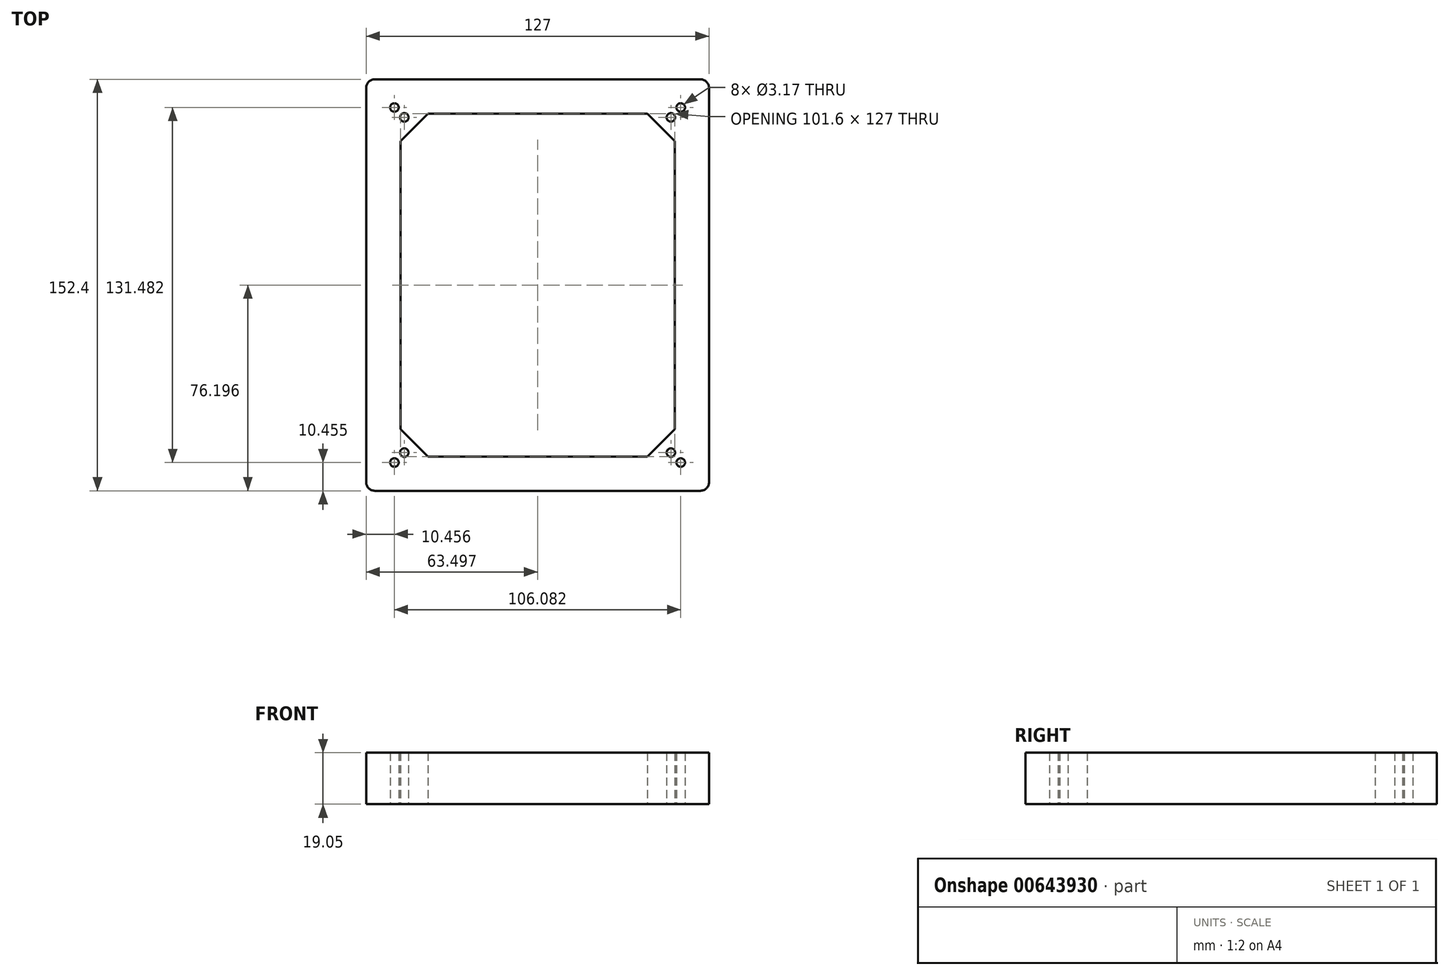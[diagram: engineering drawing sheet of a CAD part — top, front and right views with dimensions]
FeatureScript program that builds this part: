
annotation { "Feature Type Name" : "Feature", "Feature Type Description" : "" }
export const myFeature = defineFeature(function(context is Context, id is Id, definition is map)
    precondition{}
    {
        {
            var Q0;
            Q0=qCreatedBy(makeId("Top.planeOp"),FACE);
            var sketch = newSketch(context, id + "F0", { "sketchPlane" : qUnion([Q0])});
            skLineSegment(sketch, "E0.bottom", {"start": v(-60.12, 76.46) * mm, "end": v(60.53, 76.46) * mm});
            skLineSegment(sketch, "E0.top", {"start": v(-60.12, -75.94) * mm, "end": v(60.53, -75.94) * mm});
            skLineSegment(sketch, "E0.left", {"start": v(-63.3, 73.28) * mm, "end": v(-63.3, -72.77) * mm});
            skLineSegment(sketch, "E0.right", {"start": v(63.7, 73.28) * mm, "end": v(63.7, -72.77) * mm});
            skPoint(sketch, "E0.middle", {"position": v(0.2, 0.26) * mm});
            skLineSegment(sketch, "E1.bottom", {"start": v(-53.77, 70.1) * mm, "end": v(54.18, 70.1) * mm});
            skLineSegment(sketch, "E1.top", {"start": v(-53.77, -69.6) * mm, "end": v(54.18, -69.6) * mm});
            skLineSegment(sketch, "E1.left", {"start": v(-56.94, 66.93) * mm, "end": v(-56.94, -66.42) * mm});
            skLineSegment(sketch, "E1.right", {"start": v(57.36, 66.93) * mm, "end": v(57.36, -66.42) * mm});
            skLineSegment(sketch, "E2.bottom", {"start": v(-47.42, 63.76) * mm, "end": v(47.83, 63.76) * mm});
            skLineSegment(sketch, "E2.top", {"start": v(-47.42, -63.24) * mm, "end": v(48.46, -63.24) * mm});
            skLineSegment(sketch, "E2.left", {"start": v(-50.6, 60.58) * mm, "end": v(-50.6, -60.07) * mm});
            skLineSegment(sketch, "E2.right", {"start": v(51, 60.58) * mm, "end": v(51, -60.7) * mm});
            skPoint(sketch, "E3.visualSharp", {"position": v(-56.94, 70.1) * mm});
            skArc(sketch, "E3.filletArc", {"start": v(-53.77, 70.1) * mm, "mid": v(-56.01, 69.18) * mm, "end": v(-56.94, 66.93) * mm});
            skPoint(sketch, "E4.visualSharp", {"position": v(57.36, 70.1) * mm});
            skArc(sketch, "E4.filletArc", {"start": v(57.36, 66.93) * mm, "mid": v(56.43, 69.18) * mm, "end": v(54.18, 70.1) * mm});
            skPoint(sketch, "E5.visualSharp", {"position": v(57.36, -69.6) * mm});
            skArc(sketch, "E5.filletArc", {"start": v(54.18, -69.6) * mm, "mid": v(56.43, -68.66) * mm, "end": v(57.36, -66.42) * mm});
            skPoint(sketch, "E6.visualSharp", {"position": v(-56.94, -69.6) * mm});
            skArc(sketch, "E6.filletArc", {"start": v(-56.94, -66.42) * mm, "mid": v(-56.01, -68.66) * mm, "end": v(-53.77, -69.6) * mm});
            skPoint(sketch, "E7.visualSharp", {"position": v(51, 63.76) * mm});
            skArc(sketch, "E7.filletArc", {"start": v(51, 60.58) * mm, "mid": v(50.08, 62.83) * mm, "end": v(47.83, 63.76) * mm});
            skPoint(sketch, "E8.visualSharp", {"position": v(51, -63.24) * mm});
            skArc(sketch, "E8.filletArc", {"start": v(48.46, -63.24) * mm, "mid": v(50.26, -62.5) * mm, "end": v(51, -60.7) * mm});
            skPoint(sketch, "E9.visualSharp", {"position": v(-50.6, -63.24) * mm});
            skArc(sketch, "E9.filletArc", {"start": v(-50.6, -60.07) * mm, "mid": v(-49.66, -62.31) * mm, "end": v(-47.42, -63.24) * mm});
            skArc(sketch, "E10.filletArc", {"start": v(-47.42, 63.76) * mm, "mid": v(-49.66, 62.83) * mm, "end": v(-50.6, 60.58) * mm});
            skPoint(sketch, "E11.visualSharp", {"position": v(-63.3, 76.46) * mm});
            skArc(sketch, "E11.filletArc", {"start": v(-60.12, 76.46) * mm, "mid": v(-62.36, 75.53) * mm, "end": v(-63.3, 73.28) * mm});
            skPoint(sketch, "E12.visualSharp", {"position": v(63.7, 76.46) * mm});
            skArc(sketch, "E12.filletArc", {"start": v(63.7, 73.28) * mm, "mid": v(62.78, 75.53) * mm, "end": v(60.53, 76.46) * mm});
            skPoint(sketch, "E13.visualSharp", {"position": v(63.7, -75.94) * mm});
            skArc(sketch, "E13.filletArc", {"start": v(60.53, -75.94) * mm, "mid": v(62.78, -75.01) * mm, "end": v(63.7, -72.77) * mm});
            skPoint(sketch, "E14.visualSharp", {"position": v(-63.3, -75.94) * mm});
            skArc(sketch, "E14.filletArc", {"start": v(-63.3, -72.77) * mm, "mid": v(-62.36, -75.01) * mm, "end": v(-60.12, -75.94) * mm});
            skPoint(sketch, "E15", {"position": v(16.08, 63.76) * mm});
            skPoint(sketch, "E16", {"position": v(16.08, 76.46) * mm});
            skPoint(sketch, "E17", {"position": v(16.08, -63.24) * mm});
            skPoint(sketch, "E18", {"position": v(16.08, -75.94) * mm});
            skPoint(sketch, "E19", {"position": v(-15.67, 76.46) * mm});
            skPoint(sketch, "E20", {"position": v(-15.67, 63.76) * mm});
            skPoint(sketch, "E21", {"position": v(-15.67, -63.24) * mm});
            skPoint(sketch, "E22", {"position": v(-15.67, -75.94) * mm});
            skPoint(sketch, "E23", {"position": v(0.2, 76.46) * mm});
            skPoint(sketch, "E24", {"position": v(0.2, -75.94) * mm});
            skPoint(sketch, "E25", {"position": v(-63.3, 0.26) * mm});
            skPoint(sketch, "E26", {"position": v(63.7, 0.26) * mm});
            skPoint(sketch, "E27", {"position": v(63.7, 16.13) * mm});
            skPoint(sketch, "E28", {"position": v(51, 16.13) * mm});
            skPoint(sketch, "E29", {"position": v(-50.6, 16.13) * mm});
            skPoint(sketch, "E30", {"position": v(-63.3, 16.13) * mm});
            skPoint(sketch, "E31", {"position": v(63.7, -15.62) * mm});
            skPoint(sketch, "E32", {"position": v(51, -15.62) * mm});
            skPoint(sketch, "E33", {"position": v(-50.6, -15.62) * mm});
            skPoint(sketch, "E34", {"position": v(-63.3, -15.62) * mm});
            skPoint(sketch, "E35", {"position": v(40.85, 63.76) * mm});
            skPoint(sketch, "E36", {"position": v(40.85, -63.24) * mm});
            skPoint(sketch, "E37", {"position": v(-40.43, 63.76) * mm});
            skPoint(sketch, "E38", {"position": v(-40.43, -63.24) * mm});
            skPoint(sketch, "E39", {"position": v(-50.6, -53.08) * mm});
            skPoint(sketch, "E40", {"position": v(51, -53.08) * mm});
            skPoint(sketch, "E41", {"position": v(51, 53.6) * mm});
            skPoint(sketch, "E42", {"position": v(-50.6, 53.6) * mm});
            skLineSegment(sketch, "E43", {"start": v(-50.6, 53.6) * mm, "end": v(-40.43, 63.76) * mm});
            skLineSegment(sketch, "E44", {"start": v(40.85, 63.76) * mm, "end": v(51, 53.6) * mm});
            skLineSegment(sketch, "E45", {"start": v(51, -53.08) * mm, "end": v(40.85, -63.24) * mm});
            skLineSegment(sketch, "E46", {"start": v(-40.43, -63.24) * mm, "end": v(-50.6, -53.08) * mm});
            skPoint(sketch, "E47", {"position": v(-45.51, 58.68) * mm});
            skPoint(sketch, "E48", {"position": v(45.93, 58.68) * mm});
            skPoint(sketch, "E49", {"position": v(45.93, -58.16) * mm});
            skPoint(sketch, "E50", {"position": v(-45.51, -58.16) * mm});
            skPoint(sketch, "E51", {"position": v(30.37, 76.46) * mm});
            skPoint(sketch, "E52", {"position": v(30.37, 63.76) * mm});
            skPoint(sketch, "E53", {"position": v(30.37, -63.24) * mm});
            skPoint(sketch, "E54", {"position": v(30.37, -75.94) * mm});
            skPoint(sketch, "E55", {"position": v(-29.96, 76.46) * mm});
            skPoint(sketch, "E56", {"position": v(-29.96, 63.76) * mm});
            skPoint(sketch, "E57", {"position": v(-29.96, -63.24) * mm});
            skPoint(sketch, "E58", {"position": v(-29.96, -75.94) * mm});
            skPoint(sketch, "E59", {"position": v(63.7, 36.77) * mm});
            skPoint(sketch, "E60", {"position": v(51, 36.77) * mm});
            skPoint(sketch, "E61", {"position": v(-50.6, 36.77) * mm});
            skPoint(sketch, "E62", {"position": v(-63.3, 36.77) * mm});
            skPoint(sketch, "E63", {"position": v(63.7, -36.26) * mm});
            skPoint(sketch, "E64", {"position": v(51, -36.26) * mm});
            skPoint(sketch, "E65", {"position": v(-50.6, -36.26) * mm});
            skPoint(sketch, "E66", {"position": v(-63.3, -36.26) * mm});
            skPoint(sketch, "E67", {"position": v(-36.3, 76.46) * mm});
            skPoint(sketch, "E68", {"position": v(-36.3, 63.76) * mm});
            skPoint(sketch, "E69", {"position": v(-36.3, -63.24) * mm});
            skPoint(sketch, "E70", {"position": v(-36.3, -75.94) * mm});
            skPoint(sketch, "E71", {"position": v(36.72, 76.46) * mm});
            skPoint(sketch, "E72", {"position": v(36.72, 63.76) * mm});
            skPoint(sketch, "E73", {"position": v(36.72, -63.24) * mm});
            skPoint(sketch, "E74", {"position": v(36.72, -75.94) * mm});
            skPoint(sketch, "E75", {"position": v(-23.6, 76.46) * mm});
            skPoint(sketch, "E76", {"position": v(-23.6, 63.76) * mm});
            skPoint(sketch, "E77", {"position": v(24.02, 76.46) * mm});
            skPoint(sketch, "E78", {"position": v(24.02, 63.76) * mm});
            skPoint(sketch, "E79", {"position": v(24.02, -63.24) * mm});
            skPoint(sketch, "E80", {"position": v(24.02, -75.94) * mm});
            skPoint(sketch, "E81", {"position": v(-23.6, -63.24) * mm});
            skPoint(sketch, "E82", {"position": v(-23.6, -75.94) * mm});
            skPoint(sketch, "E83", {"position": v(-63.3, 43.12) * mm});
            skPoint(sketch, "E84", {"position": v(-50.6, 43.12) * mm});
            skPoint(sketch, "E85", {"position": v(51, 43.12) * mm});
            skPoint(sketch, "E86", {"position": v(63.7, 43.12) * mm});
            skPoint(sketch, "E87", {"position": v(-63.3, 30.42) * mm});
            skPoint(sketch, "E88", {"position": v(-50.6, 30.42) * mm});
            skPoint(sketch, "E89", {"position": v(51, 30.42) * mm});
            skPoint(sketch, "E90", {"position": v(63.7, 30.42) * mm});
            skPoint(sketch, "E91", {"position": v(-63.3, -29.9) * mm});
            skPoint(sketch, "E92", {"position": v(-50.6, -29.9) * mm});
            skPoint(sketch, "E93", {"position": v(51, -29.9) * mm});
            skPoint(sketch, "E94", {"position": v(63.7, -29.9) * mm});
            skPoint(sketch, "E95", {"position": v(-63.3, -42.6) * mm});
            skPoint(sketch, "E96", {"position": v(-50.6, -42.6) * mm});
            skPoint(sketch, "E97", {"position": v(51, -42.6) * mm});
            skPoint(sketch, "E98", {"position": v(63.7, -42.6) * mm});
            skLineSegment(sketch, "E99", {"start": v(57.36, 70.1) * mm, "end": v(45.93, 58.68) * mm, "construction": true});
            skLineSegment(sketch, "E100", {"start": v(57.36, -69.6) * mm, "end": v(45.93, -58.16) * mm, "construction": true});
            skLineSegment(sketch, "E101", {"start": v(-56.94, -69.6) * mm, "end": v(-45.51, -58.16) * mm, "construction": true});
            skPoint(sketch, "E102", {"position": v(53.25, 66) * mm});
            skLineSegment(sketch, "E103", {"start": v(-56.94, 70.1) * mm, "end": v(-45.51, 58.68) * mm, "construction": true});
            skPoint(sketch, "E104", {"position": v(-52.83, 66) * mm});
            skPoint(sketch, "E105", {"position": v(53.25, -65.48) * mm});
            skPoint(sketch, "E106", {"position": v(-52.83, -65.48) * mm});
            skCircle(sketch, "E107", {"center": v(-52.83, 66) * mm, "radius": 1.59 * mm});
            skCircle(sketch, "E108", {"center": v(53.25, 66) * mm, "radius": 1.59 * mm});
            skCircle(sketch, "E109", {"center": v(53.25, -65.48) * mm, "radius": 1.59 * mm});
            skCircle(sketch, "E110", {"center": v(-52.83, -65.48) * mm, "radius": 1.59 * mm});
            skPoint(sketch, "E111", {"position": v(-49.17, -61.82) * mm});
            skPoint(sketch, "E112", {"position": v(49.58, -61.82) * mm});
            skCircle(sketch, "E113", {"center": v(-49.17, -61.82) * mm, "radius": 1.59 * mm});
            skCircle(sketch, "E114", {"center": v(49.58, -61.82) * mm, "radius": 1.59 * mm});
            skPoint(sketch, "E115", {"position": v(-49.17, 62.33) * mm});
            skPoint(sketch, "E116", {"position": v(49.58, 62.33) * mm});
            skCircle(sketch, "E117", {"center": v(-49.17, 62.33) * mm, "radius": 1.59 * mm});
            skCircle(sketch, "E118", {"center": v(49.58, 62.33) * mm, "radius": 1.59 * mm});
            skSolve(sketch);
        }
        {
            var Q0;
            Q0=makeQuery(id+"F0.imprint","IMPRINT",FACE,{"disambiguationData":[TD([[makeQuery(id+"F0.imprint","IMPRINT",EDGE,{"derivedFrom":sQuery(id+"F0.wireOp",EDGE,"E0.bottom")}),-1.0]])]});
            var Q1;
            Q1=makeQuery(id+"F0.imprint","IMPRINT",FACE,{"disambiguationData":[TD([[makeQuery(id+"F0.imprint","IMPRINT",EDGE,{"derivedFrom":sQuery(id+"F0.wireOp",EDGE,"E1.bottom")}),-1.0]])]});
            var Q2;
            {var subQ5=sQuery(id+"F0.wireOp",EDGE,"E43");Q2=makeQuery(id+"F0.imprint","IMPRINT",FACE,{"disambiguationData":[TD([[makeQuery(id+"F0.imprint","IMPRINT",EDGE,{"derivedFrom":subQ5}),1.0]])]});}
            var Q3;
            {var subQ8=sQuery(id+"F0.wireOp",EDGE,"E44");Q3=makeQuery(id+"F0.imprint","IMPRINT",FACE,{"disambiguationData":[TD([[makeQuery(id+"F0.imprint","IMPRINT",EDGE,{"derivedFrom":subQ8}),1.0]])]});}
            var Q4;
            {var subQ8=sQuery(id+"F0.wireOp",EDGE,"E45");Q4=makeQuery(id+"F0.imprint","IMPRINT",FACE,{"disambiguationData":[TD([[makeQuery(id+"F0.imprint","IMPRINT",EDGE,{"derivedFrom":subQ8}),1.0]])]});}
            var Q5;
            {var subQ5=sQuery(id+"F0.wireOp",EDGE,"E46");Q5=makeQuery(id+"F0.imprint","IMPRINT",FACE,{"disambiguationData":[TD([[makeQuery(id+"F0.imprint","IMPRINT",EDGE,{"derivedFrom":subQ5}),1.0]])]});}
            extrude(context, id + "F1", {"entities" : qUnion([Q0, Q1, Q2, Q3, Q4, Q5]), "depth" : 19.05 * mm, "offsetDistance" : 25.4 * mm});
        }
    });
